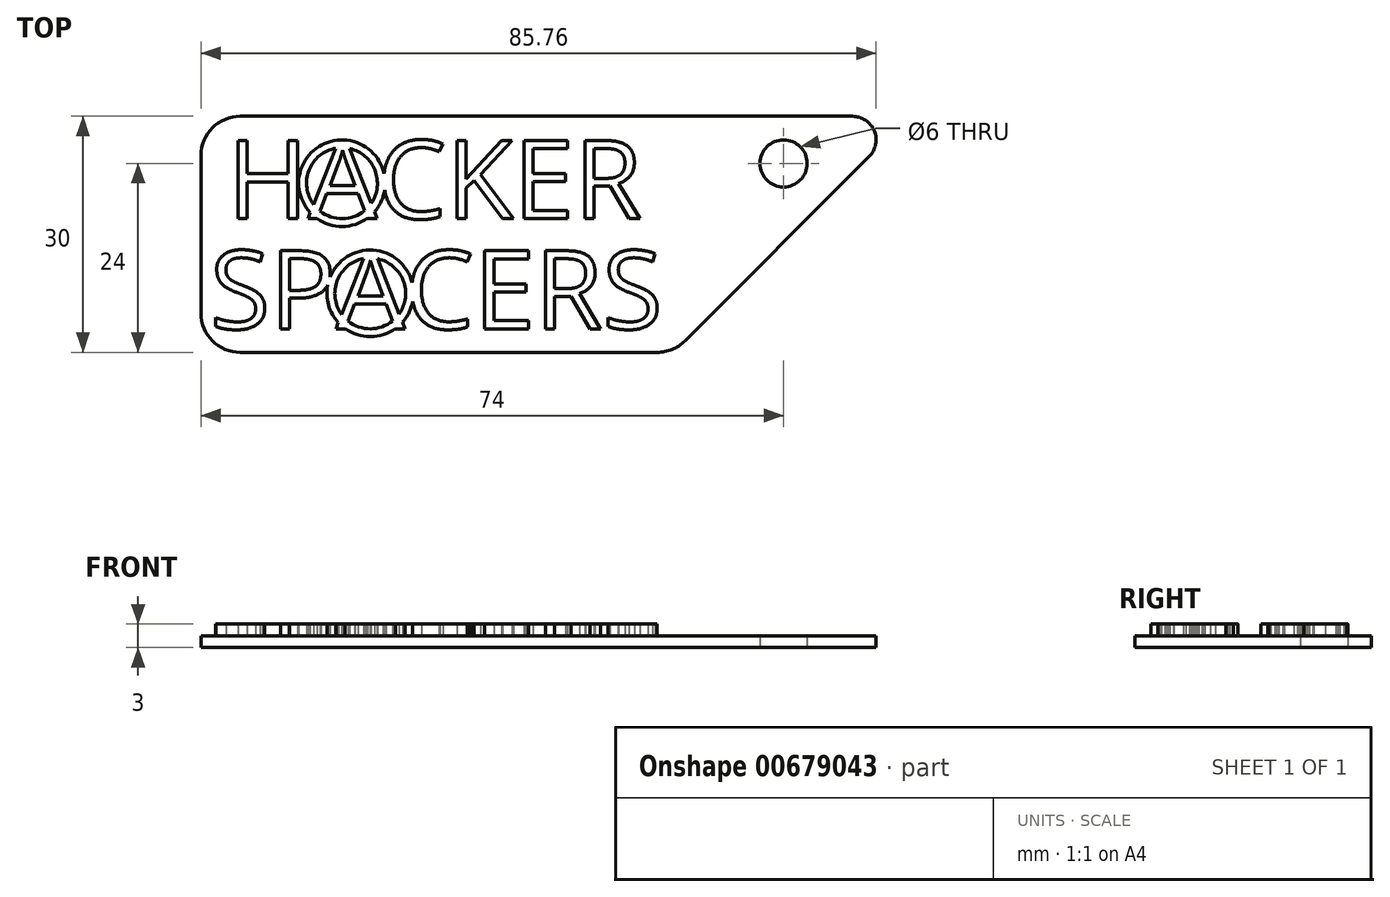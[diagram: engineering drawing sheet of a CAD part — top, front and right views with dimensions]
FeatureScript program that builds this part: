
annotation { "Feature Type Name" : "Feature", "Feature Type Description" : "" }
export const myFeature = defineFeature(function(context is Context, id is Id, definition is map)
    precondition{}
    {
        {
            var Q0;
            Q0=qCreatedBy(makeId("Top.planeOp"),FACE);
            var sketch = newSketch(context, id + "F0", { "sketchPlane" : qUnion([Q0])});
            skLineSegment(sketch, "E0.bottom", {"start": v(30, -15) * mm, "end": v(-30, -15) * mm});
            skLineSegment(sketch, "E0.top", {"start": v(30, 15) * mm, "end": v(-30, 15) * mm});
            skLineSegment(sketch, "E0.left", {"start": v(30, -15) * mm, "end": v(30, 15) * mm});
            skLineSegment(sketch, "E0.right", {"start": v(-30, -15) * mm, "end": v(-30, 15) * mm});
            skPoint(sketch, "E0.middle", {"position": v(0, 0) * mm});
            skText(sketch, "E1", { "text": "HACKER", "fontName": "OpenSans-Regular.ttf"});
            skText(sketch, "E2", { "text": "SPACERS", "fontName": "OpenSans-Regular.ttf"});
            skCircle(sketch, "E3", {"center": v(-12.09, 6.5) * mm, "radius": 5.5 * mm});
            skCircle(sketch, "E4", {"center": v(-12.09, 6.5) * mm, "radius": 4.5 * mm});
            skCircle(sketch, "E5", {"center": v(-8.5, -7.5) * mm, "radius": 5.5 * mm});
            skCircle(sketch, "E6", {"center": v(-8.5, -7.5) * mm, "radius": 4.5 * mm});
            skLineSegment(sketch, "E7", {"start": v(30, -15) * mm, "end": v(60, 15) * mm});
            skLineSegment(sketch, "E8", {"start": v(60, 15) * mm, "end": v(30, 15) * mm});
            skPoint(sketch, "E9", {"position": v(44, 9) * mm});
            const initialGuessF0  = {"E1": [-0.02665, 0.002, 1, 0, 0.01], "E2": [-0.02885, -0.012, 1, 0, 0.01]};
            skSetInitialGuess(sketch, initialGuessF0);
            skSolve(sketch);
        }
        {
            var Q0;
            Q0=makeQuery(id+"F0.imprint","IMPRINT",FACE,{"disambiguationData":[TD([[makeQuery(id+"F0.imprint","IMPRINT",EDGE,{"derivedFrom":sQuery(id+"F0.wireOp",EDGE,"E1.sketch_text.stroke-40")}),-1.0]])]});
            var Q1;
            {var subQ0=sQuery(id+"F0.wireOp",EDGE,"E4");var subQ1=sQuery(id+"F0.wireOp",EDGE,"E1.sketch_text.stroke-16");var subQ2=makeQuery(id+"F0.imprint","INTERSECT",VERTEX,{"disambiguationData":[OD(0.0)],"derivedFrom":[subQ1,subQ0]});Q1=makeQuery(id+"F0.imprint","IMPRINT",FACE,{"disambiguationData":[TD([[makeQuery(id+"F0.imprint","IMPRINT",EDGE,{"disambiguationData":[TD([[subQ2,-1.0]])],"derivedFrom":subQ1}),1.0]])]});}
            var Q2;
            {var subQ16=sQuery(id+"F0.wireOp",EDGE,"E2.sketch_text.stroke-45");Q2=makeQuery(id+"F0.imprint","IMPRINT",FACE,{"disambiguationData":[TD([[makeQuery(id+"F0.imprint","IMPRINT",EDGE,{"derivedFrom":subQ16}),1.0]])]});}
            var Q3;
            Q3=makeQuery(id+"F0.imprint","IMPRINT",FACE,{"disambiguationData":[TD([[makeQuery(id+"F0.imprint","IMPRINT",EDGE,{"derivedFrom":sQuery(id+"F0.wireOp",EDGE,"E1.sketch_text.stroke-20")}),1.0]])]});
            var Q4;
            {var subQ0=sQuery(id+"F0.wireOp",EDGE,"E5");var subQ1=sQuery(id+"F0.wireOp",EDGE,"E2.sketch_text.stroke-40");var subQ2=makeQuery(id+"F0.imprint","INTERSECT",VERTEX,{"derivedFrom":[subQ1,subQ0]});Q4=makeQuery(id+"F0.imprint","IMPRINT",FACE,{"disambiguationData":[TD([[makeQuery(id+"F0.imprint","IMPRINT",EDGE,{"disambiguationData":[TD([[subQ2,-1.0]])],"derivedFrom":subQ1}),1.0]])]});}
            var Q5;
            {var subQ0=sQuery(id+"F0.wireOp",EDGE,"E2.sketch_text.stroke-41");Q5=makeQuery(id+"F0.imprint","IMPRINT",FACE,{"disambiguationData":[TD([[makeQuery(id+"F0.imprint","IMPRINT",EDGE,{"derivedFrom":subQ0}),1.0]])]});}
            var Q6;
            Q6=makeQuery(id+"F0.imprint","IMPRINT",FACE,{"disambiguationData":[TD([[makeQuery(id+"F0.imprint","IMPRINT",EDGE,{"derivedFrom":sQuery(id+"F0.wireOp",EDGE,"E2.sketch_text.stroke-91")}),1.0]])]});
            var Q7;
            {var subQ0=sQuery(id+"F0.wireOp",EDGE,"E6");var subQ1=sQuery(id+"F0.wireOp",EDGE,"E2.sketch_text.stroke-44");var subQ2=makeQuery(id+"F0.imprint","INTERSECT",VERTEX,{"disambiguationData":[OD(0.0)],"derivedFrom":[subQ1,subQ0]});Q7=makeQuery(id+"F0.imprint","IMPRINT",FACE,{"disambiguationData":[TD([[makeQuery(id+"F0.imprint","IMPRINT",EDGE,{"disambiguationData":[TD([[subQ2,-1.0]])],"derivedFrom":subQ1}),1.0]])]});}
            var Q8;
            {var subQ12=sQuery(id+"F0.wireOp",EDGE,"E1.sketch_text.stroke-17");Q8=makeQuery(id+"F0.imprint","IMPRINT",FACE,{"disambiguationData":[TD([[makeQuery(id+"F0.imprint","IMPRINT",EDGE,{"derivedFrom":subQ12}),1.0]])]});}
            var Q9;
            {var subQ0=sQuery(id+"F0.wireOp",EDGE,"E2.sketch_text.stroke-45");Q9=makeQuery(id+"F0.imprint","IMPRINT",FACE,{"disambiguationData":[TD([[makeQuery(id+"F0.imprint","IMPRINT",EDGE,{"derivedFrom":subQ0}),-1.0]])]});}
            var Q10;
            {var subQ5=sQuery(id+"F0.wireOp",EDGE,"E3");var subQ6=sQuery(id+"F0.wireOp",EDGE,"E1.sketch_text.stroke-12");var subQ7=makeQuery(id+"F0.imprint","INTERSECT",VERTEX,{"derivedFrom":[subQ6,subQ5]});Q10=makeQuery(id+"F0.imprint","IMPRINT",FACE,{"disambiguationData":[TD([[makeQuery(id+"F0.imprint","IMPRINT",EDGE,{"disambiguationData":[TD([[subQ7,-1.0]])],"derivedFrom":subQ6}),1.0]])]});}
            var Q11;
            {var subQ0=sQuery(id+"F0.wireOp",EDGE,"E6");var subQ1=sQuery(id+"F0.wireOp",EDGE,"E2.sketch_text.stroke-42");var subQ2=makeQuery(id+"F0.imprint","INTERSECT",VERTEX,{"derivedFrom":[subQ1,subQ0]});Q11=makeQuery(id+"F0.imprint","IMPRINT",FACE,{"disambiguationData":[TD([[makeQuery(id+"F0.imprint","IMPRINT",EDGE,{"disambiguationData":[TD([[subQ2,-1.0]])],"derivedFrom":subQ1}),-1.0]])]});}
            var Q12;
            {var subQ0=sQuery(id+"F0.wireOp",EDGE,"E3");var subQ1=sQuery(id+"F0.wireOp",EDGE,"E1.sketch_text.stroke-12");var subQ2=makeQuery(id+"F0.imprint","INTERSECT",VERTEX,{"derivedFrom":[subQ1,subQ0]});Q12=makeQuery(id+"F0.imprint","IMPRINT",FACE,{"disambiguationData":[TD([[makeQuery(id+"F0.imprint","IMPRINT",EDGE,{"disambiguationData":[TD([[subQ2,-1.0]])],"derivedFrom":subQ1}),-1.0]])]});}
            var Q13;
            Q13=makeQuery(id+"F0.imprint","IMPRINT",FACE,{"disambiguationData":[TD([[makeQuery(id+"F0.imprint","IMPRINT",EDGE,{"derivedFrom":sQuery(id+"F0.wireOp",EDGE,"E0.bottom")}),-1.0]])]});
            var Q14;
            {var subQ0=sQuery(id+"F0.wireOp",EDGE,"E1.sketch_text.stroke-13");Q14=makeQuery(id+"F0.imprint","IMPRINT",FACE,{"disambiguationData":[TD([[makeQuery(id+"F0.imprint","IMPRINT",EDGE,{"derivedFrom":subQ0}),1.0]])]});}
            var Q15;
            {var subQ11=sQuery(id+"F0.wireOp",EDGE,"E1.sketch_text.stroke-13");Q15=makeQuery(id+"F0.imprint","IMPRINT",FACE,{"disambiguationData":[TD([[makeQuery(id+"F0.imprint","IMPRINT",EDGE,{"derivedFrom":subQ11}),-1.0]])]});}
            var Q16;
            Q16=makeQuery(id+"F0.imprint","IMPRINT",FACE,{"disambiguationData":[TD([[makeQuery(id+"F0.imprint","IMPRINT",EDGE,{"derivedFrom":sQuery(id+"F0.wireOp",EDGE,"E2.sketch_text.stroke-80")}),-1.0]])]});
            var Q17;
            Q17=makeQuery(id+"F0.imprint","IMPRINT",FACE,{"disambiguationData":[TD([[makeQuery(id+"F0.imprint","IMPRINT",EDGE,{"derivedFrom":sQuery(id+"F0.wireOp",EDGE,"E2.sketch_text.stroke-68")}),-1.0]])]});
            var Q18;
            Q18=makeQuery(id+"F0.imprint","IMPRINT",FACE,{"disambiguationData":[TD([[makeQuery(id+"F0.imprint","IMPRINT",EDGE,{"derivedFrom":sQuery(id+"F0.wireOp",EDGE,"E2.sketch_text.stroke-53")}),-1.0]])]});
            var Q19;
            Q19=makeQuery(id+"F0.imprint","IMPRINT",FACE,{"disambiguationData":[TD([[makeQuery(id+"F0.imprint","IMPRINT",EDGE,{"derivedFrom":sQuery(id+"F0.wireOp",EDGE,"E2.sketch_text.stroke-98")}),-1.0]])]});
            var Q20;
            {var subQ5=sQuery(id+"F0.wireOp",EDGE,"E2.sketch_text.stroke-26");Q20=makeQuery(id+"F0.imprint","IMPRINT",FACE,{"disambiguationData":[TD([[makeQuery(id+"F0.imprint","IMPRINT",EDGE,{"derivedFrom":subQ5}),-1.0]])]});}
            var Q21;
            Q21=makeQuery(id+"F0.imprint","IMPRINT",FACE,{"disambiguationData":[TD([[makeQuery(id+"F0.imprint","IMPRINT",EDGE,{"derivedFrom":sQuery(id+"F0.wireOp",EDGE,"E2.sketch_text.stroke-33")}),1.0]])]});
            var Q22;
            {var subQ0=sQuery(id+"F0.wireOp",EDGE,"E2.sketch_text.stroke-43");Q22=makeQuery(id+"F0.imprint","IMPRINT",FACE,{"disambiguationData":[TD([[makeQuery(id+"F0.imprint","IMPRINT",EDGE,{"derivedFrom":subQ0}),-1.0]])]});}
            var Q23;
            Q23=makeQuery(id+"F0.imprint","IMPRINT",FACE,{"disambiguationData":[TD([[makeQuery(id+"F0.imprint","IMPRINT",EDGE,{"derivedFrom":sQuery(id+"F0.wireOp",EDGE,"E1.sketch_text.stroke-75")}),1.0]])]});
            var Q24;
            Q24=makeQuery(id+"F0.imprint","IMPRINT",FACE,{"disambiguationData":[TD([[makeQuery(id+"F0.imprint","IMPRINT",EDGE,{"derivedFrom":sQuery(id+"F0.wireOp",EDGE,"E2.sketch_text.stroke-48")}),1.0]])]});
            var Q25;
            Q25=makeQuery(id+"F0.imprint","IMPRINT",FACE,{"disambiguationData":[TD([[makeQuery(id+"F0.imprint","IMPRINT",EDGE,{"derivedFrom":sQuery(id+"F0.wireOp",EDGE,"E2.sketch_text.stroke-0")}),-1.0]])]});
            var Q26;
            Q26=makeQuery(id+"F0.imprint","IMPRINT",FACE,{"disambiguationData":[TD([[makeQuery(id+"F0.imprint","IMPRINT",EDGE,{"derivedFrom":sQuery(id+"F0.wireOp",EDGE,"E1.sketch_text.stroke-0")}),-1.0]])]});
            var Q27;
            {var subQ0=sQuery(id+"F0.wireOp",EDGE,"E6");var subQ1=sQuery(id+"F0.wireOp",EDGE,"E2.sketch_text.stroke-46");var subQ2=makeQuery(id+"F0.imprint","INTERSECT",VERTEX,{"disambiguationData":[OD(0.0)],"derivedFrom":[subQ1,subQ0]});Q27=makeQuery(id+"F0.imprint","IMPRINT",FACE,{"disambiguationData":[TD([[makeQuery(id+"F0.imprint","IMPRINT",EDGE,{"disambiguationData":[TD([[subQ2,-1.0]])],"derivedFrom":subQ1}),1.0]])]});}
            var Q28;
            {var subQ0=sQuery(id+"F0.wireOp",EDGE,"E1.sketch_text.stroke-17");Q28=makeQuery(id+"F0.imprint","IMPRINT",FACE,{"disambiguationData":[TD([[makeQuery(id+"F0.imprint","IMPRINT",EDGE,{"derivedFrom":subQ0}),-1.0]])]});}
            var Q29;
            Q29=makeQuery(id+"F0.imprint","IMPRINT",FACE,{"disambiguationData":[TD([[makeQuery(id+"F0.imprint","IMPRINT",EDGE,{"derivedFrom":sQuery(id+"F0.wireOp",EDGE,"E1.sketch_text.stroke-64")}),-1.0]])]});
            var Q30;
            {var subQ0=sQuery(id+"F0.wireOp",EDGE,"E5");var subQ1=sQuery(id+"F0.wireOp",EDGE,"E2.sketch_text.stroke-40");var subQ2=makeQuery(id+"F0.imprint","INTERSECT",VERTEX,{"derivedFrom":[subQ1,subQ0]});Q30=makeQuery(id+"F0.imprint","IMPRINT",FACE,{"disambiguationData":[TD([[makeQuery(id+"F0.imprint","IMPRINT",EDGE,{"disambiguationData":[TD([[subQ2,-1.0]])],"derivedFrom":subQ1}),-1.0]])]});}
            var Q31;
            Q31=makeQuery(id+"F0.imprint","IMPRINT",FACE,{"disambiguationData":[TD([[makeQuery(id+"F0.imprint","IMPRINT",EDGE,{"derivedFrom":sQuery(id+"F0.wireOp",EDGE,"E1.sketch_text.stroke-52")}),-1.0]])]});
            var Q32;
            {var subQ5=sQuery(id+"F0.wireOp",EDGE,"E1.sketch_text.stroke-15");var subQ6=sQuery(id+"F0.wireOp",EDGE,"E1.sketch_text.stroke-14");var subQ7=makeQuery(id+"F0.imprint","INTERSECT",VERTEX,{"derivedFrom":[subQ6,subQ5]});Q32=makeQuery(id+"F0.imprint","IMPRINT",FACE,{"disambiguationData":[TD([[makeQuery(id+"F0.imprint","IMPRINT",EDGE,{"disambiguationData":[TD([[subQ7,1.0]])],"derivedFrom":subQ6}),-1.0]])]});}
            var Q33;
            {var subQ0=sQuery(id+"F0.wireOp",EDGE,"E2.sketch_text.stroke-41");Q33=makeQuery(id+"F0.imprint","IMPRINT",FACE,{"disambiguationData":[TD([[makeQuery(id+"F0.imprint","IMPRINT",EDGE,{"derivedFrom":subQ0}),-1.0]])]});}
            var Q34;
            {var subQ0=sQuery(id+"F0.wireOp",EDGE,"E4");var subQ1=sQuery(id+"F0.wireOp",EDGE,"E1.sketch_text.stroke-18");var subQ2=makeQuery(id+"F0.imprint","INTERSECT",VERTEX,{"disambiguationData":[OD(0.0)],"derivedFrom":[subQ1,subQ0]});Q34=makeQuery(id+"F0.imprint","IMPRINT",FACE,{"disambiguationData":[TD([[makeQuery(id+"F0.imprint","IMPRINT",EDGE,{"disambiguationData":[TD([[subQ2,-1.0]])],"derivedFrom":subQ1}),1.0]])]});}
            var Q35;
            Q35=makeQuery(id+"F0.imprint","IMPRINT",FACE,{"disambiguationData":[TD([[makeQuery(id+"F0.imprint","IMPRINT",EDGE,{"derivedFrom":sQuery(id+"F0.wireOp",EDGE,"E1.sketch_text.stroke-25")}),-1.0]])]});
            var Q36;
            {var subQ0=sQuery(id+"F0.wireOp",EDGE,"E1.sketch_text.stroke-16");var subQ1=sQuery(id+"F0.wireOp",EDGE,"E1.sketch_text.stroke-15");var subQ2=makeQuery(id+"F0.imprint","INTERSECT",VERTEX,{"derivedFrom":[subQ1,subQ0]});Q36=makeQuery(id+"F0.imprint","IMPRINT",FACE,{"disambiguationData":[TD([[makeQuery(id+"F0.imprint","IMPRINT",EDGE,{"disambiguationData":[TD([[subQ2,1.0]])],"derivedFrom":subQ1}),-1.0]])]});}
            var Q37;
            {var subQ0=sQuery(id+"F0.wireOp",EDGE,"E1.sketch_text.stroke-34");var subQ1=sQuery(id+"F0.wireOp",EDGE,"E1.sketch_text.stroke-33");var subQ2=makeQuery(id+"F0.imprint","INTERSECT",VERTEX,{"derivedFrom":[subQ1,subQ0]});Q37=makeQuery(id+"F0.imprint","IMPRINT",FACE,{"disambiguationData":[TD([[makeQuery(id+"F0.imprint","IMPRINT",EDGE,{"disambiguationData":[TD([[subQ2,1.0]])],"derivedFrom":subQ1}),-1.0]])]});}
            var Q38;
            {var subQ0=sQuery(id+"F0.wireOp",EDGE,"E2.sketch_text.stroke-62");var subQ1=sQuery(id+"F0.wireOp",EDGE,"E2.sketch_text.stroke-61");var subQ2=makeQuery(id+"F0.imprint","INTERSECT",VERTEX,{"derivedFrom":[subQ1,subQ0]});Q38=makeQuery(id+"F0.imprint","IMPRINT",FACE,{"disambiguationData":[TD([[makeQuery(id+"F0.imprint","IMPRINT",EDGE,{"disambiguationData":[TD([[subQ2,1.0]])],"derivedFrom":subQ1}),-1.0]])]});}
            var Q39;
            {var subQ0=sQuery(id+"F0.wireOp",EDGE,"E2.sketch_text.stroke-47");Q39=makeQuery(id+"F0.imprint","IMPRINT",FACE,{"disambiguationData":[TD([[makeQuery(id+"F0.imprint","IMPRINT",EDGE,{"derivedFrom":subQ0}),-1.0]])]});}
            var Q40;
            {var subQ0=sQuery(id+"F0.wireOp",EDGE,"E1.sketch_text.stroke-19");Q40=makeQuery(id+"F0.imprint","IMPRINT",FACE,{"disambiguationData":[TD([[makeQuery(id+"F0.imprint","IMPRINT",EDGE,{"derivedFrom":subQ0}),-1.0]])]});}
            var Q41;
            {var subQ0=sQuery(id+"F0.wireOp",EDGE,"E5");var subQ1=sQuery(id+"F0.wireOp",EDGE,"E2.sketch_text.stroke-25");var subQ2=makeQuery(id+"F0.imprint","INTERSECT",VERTEX,{"disambiguationData":[OD(0.0)],"derivedFrom":[subQ1,subQ0]});Q41=makeQuery(id+"F0.imprint","IMPRINT",FACE,{"disambiguationData":[TD([[makeQuery(id+"F0.imprint","IMPRINT",EDGE,{"disambiguationData":[TD([[subQ2,-1.0]])],"derivedFrom":subQ1}),-1.0]])]});}
            var Q42;
            Q42=makeQuery(id+"F0.imprint","IMPRINT",FACE,{"disambiguationData":[TD([[makeQuery(id+"F0.imprint","IMPRINT",EDGE,{"derivedFrom":sQuery(id+"F0.wireOp",EDGE,"E0.left")}),-1.0]])]});
            extrude(context, id + "F1", {"entities" : qUnion([Q0, Q1, Q2, Q3, Q4, Q5, Q6, Q7, Q8, Q9, Q10, Q11, Q12, Q13, Q14, Q15, Q16, Q17, Q18, Q19, Q20, Q21, Q22, Q23, Q24, Q25, Q26, Q27, Q28, Q29, Q30, Q31, Q32, Q33, Q34, Q35, Q36, Q37, Q38, Q39, Q40, Q41, Q42]), "depth" : 1.5 * mm, "offsetDistance" : 25 * mm});
        }
        {
            var Q0;
            {var subQ0=sQuery(id+"F0.wireOp",EDGE,"E5");var subQ1=sQuery(id+"F0.wireOp",EDGE,"E2.sketch_text.stroke-25");var subQ2=makeQuery(id+"F0.imprint","INTERSECT",VERTEX,{"disambiguationData":[OD(0.0)],"derivedFrom":[subQ1,subQ0]});Q0=makeQuery(id+"F0.imprint","IMPRINT",FACE,{"disambiguationData":[TD([[makeQuery(id+"F0.imprint","IMPRINT",EDGE,{"disambiguationData":[TD([[subQ2,-1.0]])],"derivedFrom":subQ1}),-1.0]])]});}
            var Q1;
            {var subQ16=sQuery(id+"F0.wireOp",EDGE,"E2.sketch_text.stroke-45");Q1=makeQuery(id+"F0.imprint","IMPRINT",FACE,{"disambiguationData":[TD([[makeQuery(id+"F0.imprint","IMPRINT",EDGE,{"derivedFrom":subQ16}),1.0]])]});}
            var Q2;
            {var subQ5=sQuery(id+"F0.wireOp",EDGE,"E2.sketch_text.stroke-26");Q2=makeQuery(id+"F0.imprint","IMPRINT",FACE,{"disambiguationData":[TD([[makeQuery(id+"F0.imprint","IMPRINT",EDGE,{"derivedFrom":subQ5}),-1.0]])]});}
            var Q3;
            {var subQ0=sQuery(id+"F0.wireOp",EDGE,"E2.sketch_text.stroke-45");Q3=makeQuery(id+"F0.imprint","IMPRINT",FACE,{"disambiguationData":[TD([[makeQuery(id+"F0.imprint","IMPRINT",EDGE,{"derivedFrom":subQ0}),-1.0]])]});}
            var Q4;
            {var subQ0=sQuery(id+"F0.wireOp",EDGE,"E2.sketch_text.stroke-41");Q4=makeQuery(id+"F0.imprint","IMPRINT",FACE,{"disambiguationData":[TD([[makeQuery(id+"F0.imprint","IMPRINT",EDGE,{"derivedFrom":subQ0}),-1.0]])]});}
            var Q5;
            {var subQ0=sQuery(id+"F0.wireOp",EDGE,"E5");var subQ1=sQuery(id+"F0.wireOp",EDGE,"E2.sketch_text.stroke-40");var subQ2=makeQuery(id+"F0.imprint","INTERSECT",VERTEX,{"derivedFrom":[subQ1,subQ0]});Q5=makeQuery(id+"F0.imprint","IMPRINT",FACE,{"disambiguationData":[TD([[makeQuery(id+"F0.imprint","IMPRINT",EDGE,{"disambiguationData":[TD([[subQ2,-1.0]])],"derivedFrom":subQ1}),-1.0]])]});}
            var Q6;
            {var subQ0=sQuery(id+"F0.wireOp",EDGE,"E2.sketch_text.stroke-47");Q6=makeQuery(id+"F0.imprint","IMPRINT",FACE,{"disambiguationData":[TD([[makeQuery(id+"F0.imprint","IMPRINT",EDGE,{"derivedFrom":subQ0}),-1.0]])]});}
            var Q7;
            {var subQ0=sQuery(id+"F0.wireOp",EDGE,"E2.sketch_text.stroke-43");Q7=makeQuery(id+"F0.imprint","IMPRINT",FACE,{"disambiguationData":[TD([[makeQuery(id+"F0.imprint","IMPRINT",EDGE,{"derivedFrom":subQ0}),-1.0]])]});}
            var Q8;
            {var subQ0=sQuery(id+"F0.wireOp",EDGE,"E6");var subQ1=sQuery(id+"F0.wireOp",EDGE,"E2.sketch_text.stroke-42");var subQ2=makeQuery(id+"F0.imprint","INTERSECT",VERTEX,{"derivedFrom":[subQ1,subQ0]});Q8=makeQuery(id+"F0.imprint","IMPRINT",FACE,{"disambiguationData":[TD([[makeQuery(id+"F0.imprint","IMPRINT",EDGE,{"disambiguationData":[TD([[subQ2,-1.0]])],"derivedFrom":subQ1}),-1.0]])]});}
            var Q9;
            {var subQ0=sQuery(id+"F0.wireOp",EDGE,"E5");var subQ1=sQuery(id+"F0.wireOp",EDGE,"E2.sketch_text.stroke-40");var subQ2=makeQuery(id+"F0.imprint","INTERSECT",VERTEX,{"derivedFrom":[subQ1,subQ0]});Q9=makeQuery(id+"F0.imprint","IMPRINT",FACE,{"disambiguationData":[TD([[makeQuery(id+"F0.imprint","IMPRINT",EDGE,{"disambiguationData":[TD([[subQ2,-1.0]])],"derivedFrom":subQ1}),1.0]])]});}
            extrude(context, id + "F2", {"entities" : qUnion([Q0, Q1, Q2, Q3, Q4, Q5, Q6, Q7, Q8, Q9]), "operationType" : NewBodyOperationType.ADD, "depth" : 3 * mm, "offsetDistance" : 25 * mm});
        }
        {
            var Q0;
            Q0=makeQuery(id+"F0.imprint","IMPRINT",FACE,{"disambiguationData":[TD([[makeQuery(id+"F0.imprint","IMPRINT",EDGE,{"derivedFrom":sQuery(id+"F0.wireOp",EDGE,"E2.sketch_text.stroke-53")}),-1.0]])]});
            var Q1;
            Q1=makeQuery(id+"F0.imprint","IMPRINT",FACE,{"disambiguationData":[TD([[makeQuery(id+"F0.imprint","IMPRINT",EDGE,{"derivedFrom":sQuery(id+"F0.wireOp",EDGE,"E2.sketch_text.stroke-68")}),-1.0]])]});
            var Q2;
            Q2=makeQuery(id+"F0.imprint","IMPRINT",FACE,{"disambiguationData":[TD([[makeQuery(id+"F0.imprint","IMPRINT",EDGE,{"derivedFrom":sQuery(id+"F0.wireOp",EDGE,"E2.sketch_text.stroke-80")}),-1.0]])]});
            var Q3;
            Q3=makeQuery(id+"F0.imprint","IMPRINT",FACE,{"disambiguationData":[TD([[makeQuery(id+"F0.imprint","IMPRINT",EDGE,{"derivedFrom":sQuery(id+"F0.wireOp",EDGE,"E2.sketch_text.stroke-98")}),-1.0]])]});
            var Q4;
            Q4=makeQuery(id+"F0.imprint","IMPRINT",FACE,{"disambiguationData":[TD([[makeQuery(id+"F0.imprint","IMPRINT",EDGE,{"derivedFrom":sQuery(id+"F0.wireOp",EDGE,"E2.sketch_text.stroke-0")}),-1.0]])]});
            var Q5;
            {var subQ0=sQuery(id+"F0.wireOp",EDGE,"E2.sketch_text.stroke-62");var subQ1=sQuery(id+"F0.wireOp",EDGE,"E2.sketch_text.stroke-61");var subQ2=makeQuery(id+"F0.imprint","INTERSECT",VERTEX,{"derivedFrom":[subQ1,subQ0]});Q5=makeQuery(id+"F0.imprint","IMPRINT",FACE,{"disambiguationData":[TD([[makeQuery(id+"F0.imprint","IMPRINT",EDGE,{"disambiguationData":[TD([[subQ2,1.0]])],"derivedFrom":subQ1}),-1.0]])]});}
            extrude(context, id + "F3", {"entities" : qUnion([Q0, Q1, Q2, Q3, Q4, Q5]), "operationType" : NewBodyOperationType.ADD, "depth" : 3 * mm, "offsetDistance" : 25 * mm});
        }
        {
            var Q0;
            Q0=makeQuery(id+"F0.imprint","IMPRINT",FACE,{"disambiguationData":[TD([[makeQuery(id+"F0.imprint","IMPRINT",EDGE,{"derivedFrom":sQuery(id+"F0.wireOp",EDGE,"E1.sketch_text.stroke-0")}),-1.0]])]});
            var Q1;
            {var subQ12=sQuery(id+"F0.wireOp",EDGE,"E1.sketch_text.stroke-17");Q1=makeQuery(id+"F0.imprint","IMPRINT",FACE,{"disambiguationData":[TD([[makeQuery(id+"F0.imprint","IMPRINT",EDGE,{"derivedFrom":subQ12}),1.0]])]});}
            var Q2;
            {var subQ11=sQuery(id+"F0.wireOp",EDGE,"E1.sketch_text.stroke-13");Q2=makeQuery(id+"F0.imprint","IMPRINT",FACE,{"disambiguationData":[TD([[makeQuery(id+"F0.imprint","IMPRINT",EDGE,{"derivedFrom":subQ11}),-1.0]])]});}
            var Q3;
            {var subQ0=sQuery(id+"F0.wireOp",EDGE,"E1.sketch_text.stroke-17");Q3=makeQuery(id+"F0.imprint","IMPRINT",FACE,{"disambiguationData":[TD([[makeQuery(id+"F0.imprint","IMPRINT",EDGE,{"derivedFrom":subQ0}),-1.0]])]});}
            var Q4;
            {var subQ0=sQuery(id+"F0.wireOp",EDGE,"E3");var subQ1=sQuery(id+"F0.wireOp",EDGE,"E1.sketch_text.stroke-12");var subQ2=makeQuery(id+"F0.imprint","INTERSECT",VERTEX,{"derivedFrom":[subQ1,subQ0]});Q4=makeQuery(id+"F0.imprint","IMPRINT",FACE,{"disambiguationData":[TD([[makeQuery(id+"F0.imprint","IMPRINT",EDGE,{"disambiguationData":[TD([[subQ2,-1.0]])],"derivedFrom":subQ1}),-1.0]])]});}
            var Q5;
            {var subQ0=sQuery(id+"F0.wireOp",EDGE,"E1.sketch_text.stroke-19");Q5=makeQuery(id+"F0.imprint","IMPRINT",FACE,{"disambiguationData":[TD([[makeQuery(id+"F0.imprint","IMPRINT",EDGE,{"derivedFrom":subQ0}),-1.0]])]});}
            var Q6;
            {var subQ5=sQuery(id+"F0.wireOp",EDGE,"E3");var subQ6=sQuery(id+"F0.wireOp",EDGE,"E1.sketch_text.stroke-12");var subQ7=makeQuery(id+"F0.imprint","INTERSECT",VERTEX,{"derivedFrom":[subQ6,subQ5]});Q6=makeQuery(id+"F0.imprint","IMPRINT",FACE,{"disambiguationData":[TD([[makeQuery(id+"F0.imprint","IMPRINT",EDGE,{"disambiguationData":[TD([[subQ7,-1.0]])],"derivedFrom":subQ6}),1.0]])]});}
            var Q7;
            {var subQ5=sQuery(id+"F0.wireOp",EDGE,"E1.sketch_text.stroke-15");var subQ6=sQuery(id+"F0.wireOp",EDGE,"E1.sketch_text.stroke-14");var subQ7=makeQuery(id+"F0.imprint","INTERSECT",VERTEX,{"derivedFrom":[subQ6,subQ5]});Q7=makeQuery(id+"F0.imprint","IMPRINT",FACE,{"disambiguationData":[TD([[makeQuery(id+"F0.imprint","IMPRINT",EDGE,{"disambiguationData":[TD([[subQ7,1.0]])],"derivedFrom":subQ6}),-1.0]])]});}
            var Q8;
            {var subQ0=sQuery(id+"F0.wireOp",EDGE,"E1.sketch_text.stroke-16");var subQ1=sQuery(id+"F0.wireOp",EDGE,"E1.sketch_text.stroke-15");var subQ2=makeQuery(id+"F0.imprint","INTERSECT",VERTEX,{"derivedFrom":[subQ1,subQ0]});Q8=makeQuery(id+"F0.imprint","IMPRINT",FACE,{"disambiguationData":[TD([[makeQuery(id+"F0.imprint","IMPRINT",EDGE,{"disambiguationData":[TD([[subQ2,1.0]])],"derivedFrom":subQ1}),-1.0]])]});}
            var Q9;
            {var subQ0=sQuery(id+"F0.wireOp",EDGE,"E1.sketch_text.stroke-34");var subQ1=sQuery(id+"F0.wireOp",EDGE,"E1.sketch_text.stroke-33");var subQ2=makeQuery(id+"F0.imprint","INTERSECT",VERTEX,{"derivedFrom":[subQ1,subQ0]});Q9=makeQuery(id+"F0.imprint","IMPRINT",FACE,{"disambiguationData":[TD([[makeQuery(id+"F0.imprint","IMPRINT",EDGE,{"disambiguationData":[TD([[subQ2,1.0]])],"derivedFrom":subQ1}),-1.0]])]});}
            var Q10;
            Q10=makeQuery(id+"F0.imprint","IMPRINT",FACE,{"disambiguationData":[TD([[makeQuery(id+"F0.imprint","IMPRINT",EDGE,{"derivedFrom":sQuery(id+"F0.wireOp",EDGE,"E1.sketch_text.stroke-25")}),-1.0]])]});
            var Q11;
            Q11=makeQuery(id+"F0.imprint","IMPRINT",FACE,{"disambiguationData":[TD([[makeQuery(id+"F0.imprint","IMPRINT",EDGE,{"derivedFrom":sQuery(id+"F0.wireOp",EDGE,"E1.sketch_text.stroke-40")}),-1.0]])]});
            var Q12;
            Q12=makeQuery(id+"F0.imprint","IMPRINT",FACE,{"disambiguationData":[TD([[makeQuery(id+"F0.imprint","IMPRINT",EDGE,{"derivedFrom":sQuery(id+"F0.wireOp",EDGE,"E1.sketch_text.stroke-52")}),-1.0]])]});
            var Q13;
            Q13=makeQuery(id+"F0.imprint","IMPRINT",FACE,{"disambiguationData":[TD([[makeQuery(id+"F0.imprint","IMPRINT",EDGE,{"derivedFrom":sQuery(id+"F0.wireOp",EDGE,"E1.sketch_text.stroke-64")}),-1.0]])]});
            extrude(context, id + "F4", {"entities" : qUnion([Q0, Q1, Q2, Q3, Q4, Q5, Q6, Q7, Q8, Q9, Q10, Q11, Q12, Q13]), "operationType" : NewBodyOperationType.ADD, "depth" : 3 * mm, "offsetDistance" : 25 * mm});
        }
        {
            var Q0;
            Q0=makeQuery(id+"F1.opExtrude","SWEPT_EDGE",EDGE,{"disambiguationData":[OSD([sQuery(id+"F0.wireOp",EDGE,"E0.bottom"),sQuery(id+"F0.wireOp",EDGE,"E0.right")])]});
            var Q1;
            Q1=makeQuery(id+"F1.opExtrude","SWEPT_EDGE",EDGE,{"disambiguationData":[OSD([sQuery(id+"F0.wireOp",EDGE,"E0.top"),sQuery(id+"F0.wireOp",EDGE,"E0.right")])]});
            var Q2;
            Q2=makeQuery(id+"F1.opExtrude","SWEPT_EDGE",EDGE,{"disambiguationData":[OSD([sQuery(id+"F0.wireOp",EDGE,"E0.bottom"),sQuery(id+"F0.wireOp",EDGE,"E0.left"),sQuery(id+"F0.wireOp",EDGE,"E7")])]});
            fillet(context, id + "F5", {"entities" : qUnion([Q0, Q1, Q2]), "radius" : 5 * mm, "tangentPropagation" : true, "allowEdgeOverflow" : false});
        }
        {
            var Q0;
            Q0=makeQuery(id+"F1.opExtrude","SWEPT_EDGE",EDGE,{"disambiguationData":[OSD([sQuery(id+"F0.wireOp",EDGE,"E7"),sQuery(id+"F0.wireOp",EDGE,"E8")])]});
            fillet(context, id + "F6", {"entities" : qUnion([Q0]), "radius" : 3 * mm, "tangentPropagation" : true, "allowEdgeOverflow" : false});
        }
        {
            var Q0;
            Q0=sQuery(id+"F0.wireOp",VERTEX,"E9");
            var Q1;
            Q1=makeQuery(id+"F1.opExtrude","SWEPT_BODY",BODY,{"disambiguationData":[OSD([sQuery(id+"F0.wireOp",EDGE,"E0.bottom"),sQuery(id+"F0.wireOp",EDGE,"E0.top"),sQuery(id+"F0.wireOp",EDGE,"E0.right"),sQuery(id+"F0.wireOp",EDGE,"E7"),sQuery(id+"F0.wireOp",EDGE,"E8")])]});
            hole(context, id + "F7", {"style" : HoleStyle.SIMPLE, "endStyle" : HoleEndStyle.THROUGH, "oppositeDirection" : true, "holeDiameter" : 6 * mm, "majorDiameter" : 5 * mm, "isTappedThrough" : true, "tappedDepth" : 12 * mm, "tapClearance" : 3, "locations" : qUnion([Q0]), "scope" : qUnion([Q1])});
        }
    });
